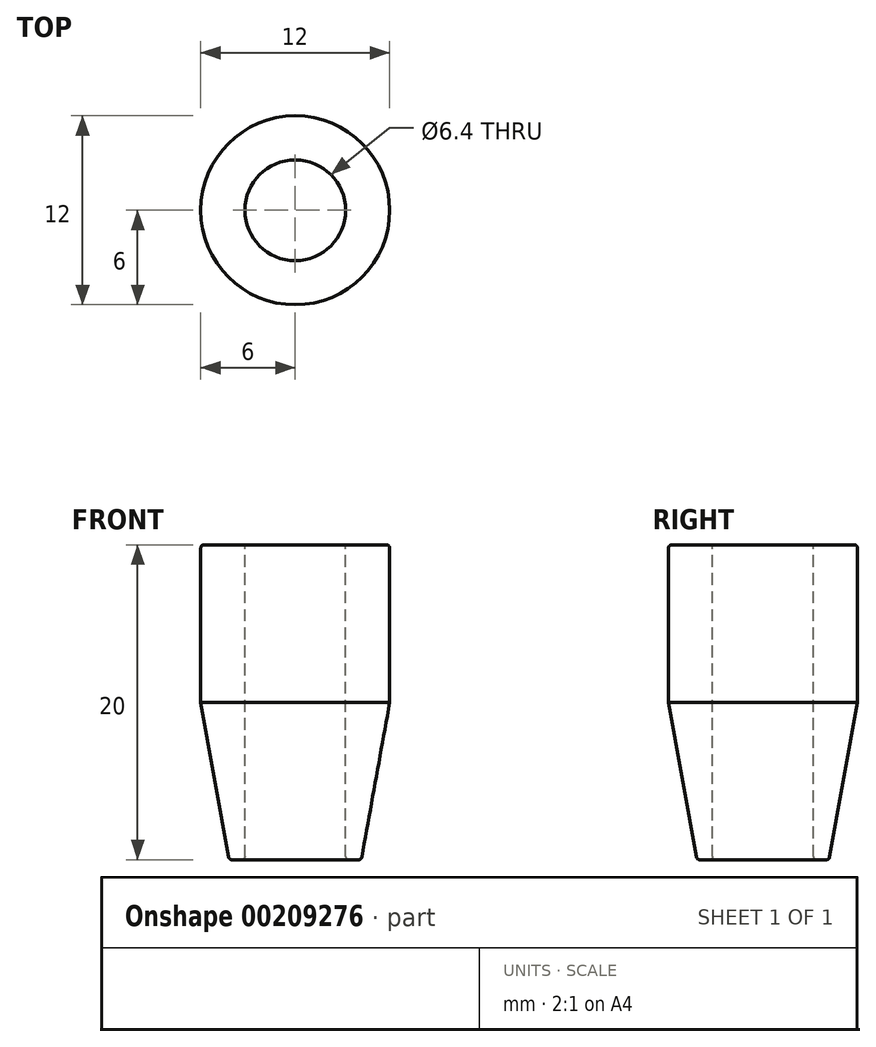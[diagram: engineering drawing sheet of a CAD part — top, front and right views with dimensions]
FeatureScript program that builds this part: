
annotation { "Feature Type Name" : "Feature", "Feature Type Description" : "" }
export const myFeature = defineFeature(function(context is Context, id is Id, definition is map)
    precondition{}
    {
        {
            var Q0;
            Q0=qCreatedBy(makeId("Front.planeOp"),FACE);
            var sketch = newSketch(context, id + "F0", { "sketchPlane" : qUnion([Q0])});
            skLineSegment(sketch, "E0", {"start": v(0, 0) * mm, "end": v(0, -10) * mm, "construction": true});
            skLineSegment(sketch, "E1", {"start": v(-3.2, -10) * mm, "end": v(-3.2, 0) * mm});
            skLineSegment(sketch, "E2", {"start": v(-3.2, -10) * mm, "end": v(-4.2, -10) * mm});
            skLineSegment(sketch, "E3", {"start": v(-4.2, -10) * mm, "end": v(-6, 0) * mm});
            skLineSegment(sketch, "E4.bottom", {"start": v(-3.2, 0) * mm, "end": v(-6, 0) * mm});
            skLineSegment(sketch, "E4.top", {"start": v(-3.2, 10) * mm, "end": v(-6, 10) * mm});
            skLineSegment(sketch, "E4.left", {"start": v(-3.2, 0) * mm, "end": v(-3.2, 10) * mm});
            skLineSegment(sketch, "E4.right", {"start": v(-6, 0) * mm, "end": v(-6, 10) * mm});
            skLineSegment(sketch, "E5", {"start": v(0, 0) * mm, "end": v(-3.2, 0) * mm, "construction": true});
            skSolve(sketch);
        }
        {
            var Q0;
            Q0=makeQuery(id+"F0.imprint","IMPRINT",FACE,{"disambiguationData":[TD([[makeQuery(id+"F0.imprint","IMPRINT",EDGE,{"derivedFrom":sQuery(id+"F0.wireOp",EDGE,"E4.bottom")}),-1.0]])]});
            var Q1;
            Q1=makeQuery(id+"F0.imprint","IMPRINT",FACE,{"disambiguationData":[TD([[makeQuery(id+"F0.imprint","IMPRINT",EDGE,{"derivedFrom":sQuery(id+"F0.wireOp",EDGE,"E1")}),1.0]])]});
            var Q2;
            Q2=sQuery(id+"F0.wireOp",EDGE,"E0");
            revolve(context, id + "F1", {"entities" : qUnion([Q0, Q1]), "axis" : qUnion([Q2]), "revolveType" : RevolveType.FULL});
        }
        {
            var Q0;
            Q0=makeQuery(id+"F1.opRevolve","SWEPT_EDGE",EDGE,{"disambiguationData":[OSD([sQuery(id+"F0.wireOp",EDGE,"E2"),sQuery(id+"F0.wireOp",EDGE,"E3")])]});
            var Q1;
            Q1=makeQuery(id+"F1.opRevolve","SWEPT_EDGE",EDGE,{"disambiguationData":[OSD([sQuery(id+"F0.wireOp",EDGE,"E4.top"),sQuery(id+"F0.wireOp",EDGE,"E4.right")])]});
            var Q2;
            Q2=makeQuery(id+"F1.opRevolve","SWEPT_EDGE",EDGE,{"disambiguationData":[OSD([sQuery(id+"F0.wireOp",EDGE,"E1"),sQuery(id+"F0.wireOp",EDGE,"E2")])]});
            fillet(context, id + "F2", {"entities" : qUnion([Q0, Q1, Q2]), "radius" : .2 * mm, "tangentPropagation" : true, "allowEdgeOverflow" : false});
        }
    });
